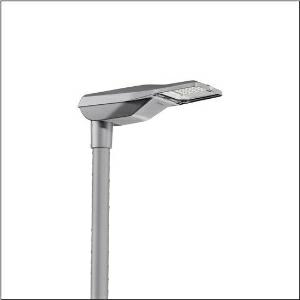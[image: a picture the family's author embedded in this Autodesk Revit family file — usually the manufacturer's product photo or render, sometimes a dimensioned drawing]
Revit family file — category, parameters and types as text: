
# Revit family: streetlight_sl_21_iq_micro___st1_0a_5xe1d41g08db_b7c0
name_source: partatom
category: Lighting Fixtures
units: mm (PartAtom-declared; Revit-internal decimal feet)

## family parameters
Cut with Voids When Loaded = No
Host = Face
Light Source = No
Part Type = Normal
Room Calculation Point = No
Round Connector Dimension = Use Diameter
Shared = No

## types (1)
- --- (1 x LED, 5010 lm, 36.4 W, 4000K)
    Apparent Load = 36 VA
    CIE Flux Codes = 37 72 97 100 100
    Color Rendering = 70
    Color Temperature = 4000K
    Default Elevation = 1800 mm
    Description = Streetlight SL 21 iQ micro, mast luminaire, primary light control with lens, of PMMA, primary optical cover: cover, of toughened safety glass, transparent, light distribution: ST1.0a, light emission: direct distribution, primary light characteristic: asymmetric, installation type: post-top, side-entry, LED, High Power LED, rated luminous flux: 5.010lm, luminous efficacy: 138lm/W, light colour: 740, colour temperature: 4000K, control gear: iQ Street-Remote, control: Street-Remote, Auto-Match, Temp-Guard, Lumen-Switch, Night-Set, Smart-Wire, Light-Fading, Desk-Remote (wireless, voltage-free reading and setting of iQ features in the workshop via application-optimized NFC function/RFID function), optimised constant luminous flux control (CLO 2.0), pre-setting: linear dimming characteristic, mains connection: 220..240V, AC, 50/60Hz, start of lifetime: 36W, end of service life: 38W, reduction: 16W, luminaire housing, of diecast aluminium, powder-coated, Siteco® metallic grey (DB 702S), corrosivity category C5 mid according to DIN EN ISO 12944, please order mast flange separately, inclination adjustable: 0°, 5°, 10°, 15°, sealing non-destructively replaceable, multi-level sealing system, length: 528mm, width: 235mm, height: 110mm, mast flange for spigot size: 42mm (side-entry): 5XC10008XM4, 60/48mm (side-entry/post-top): 5XC10108XM2, 76/60mm (side-entry/post-top): 5XC10108XM1, protection rating (complete): IP66, insulation class (complete): insulation class II (safety insulation), certification: CE, ENEC, ENEC+, VDE, impact resistance: IK10, permissible operating ambient temperature for outdoor applications: -40..+50°C, standard-compliant lighting for roads and squares, packaging unit: 1 piece

Light Distribution: ST1.0a
    Height = 110 mm
    Lamp = 1 x LED
    Lamp Light Flux = 5010 lm
    Lamp Power = 36.4 W
    Lamp count = 1
    Length = 528 mm
    Luminous efficacy = 138 lm/W
    Manufacturer = Siteco
    ModVariant = No
    Model = 5XE1D41G08DB
    Number of Poles = 1
    OnlyDefault = Yes
    Power Factor = 1
    Product Name = Streetlight SL 21 iQ micro | ST1.0a
    Product group = mast luminaire | pylon top
    ProductGroupID = 6100
    Protection Class = Protection class II
    Protection Degree = IP 66
    RLX_Detail_Level = 1
    RLX_Emergency_Light_Flux = 0 lm
    RLX_Emergency_Type = 0
    RLX_Emergency_Type_DB = No
    RlxData = <blob elided: 99181 chars, md5=03b08fb9>
    Socket = socket
    Standby Power = 0 W
    System Light Flux = 5010 lm
    System Power = 36 W
    Type Comments = factory setting: luminous flux: 100 % | dim-lin: 254 | 715 mA
    Type Image = l_1006881.jpg
    URL = http://relux.com
    VarID = @adj_177391
    Voltage = 0 V
    Weight = 0.00 kg
    Width = 235 mm

## geometry (parser evidence)
native form markers: Blend x4, Sweep x12
no freeform markers — native parametric forms only
